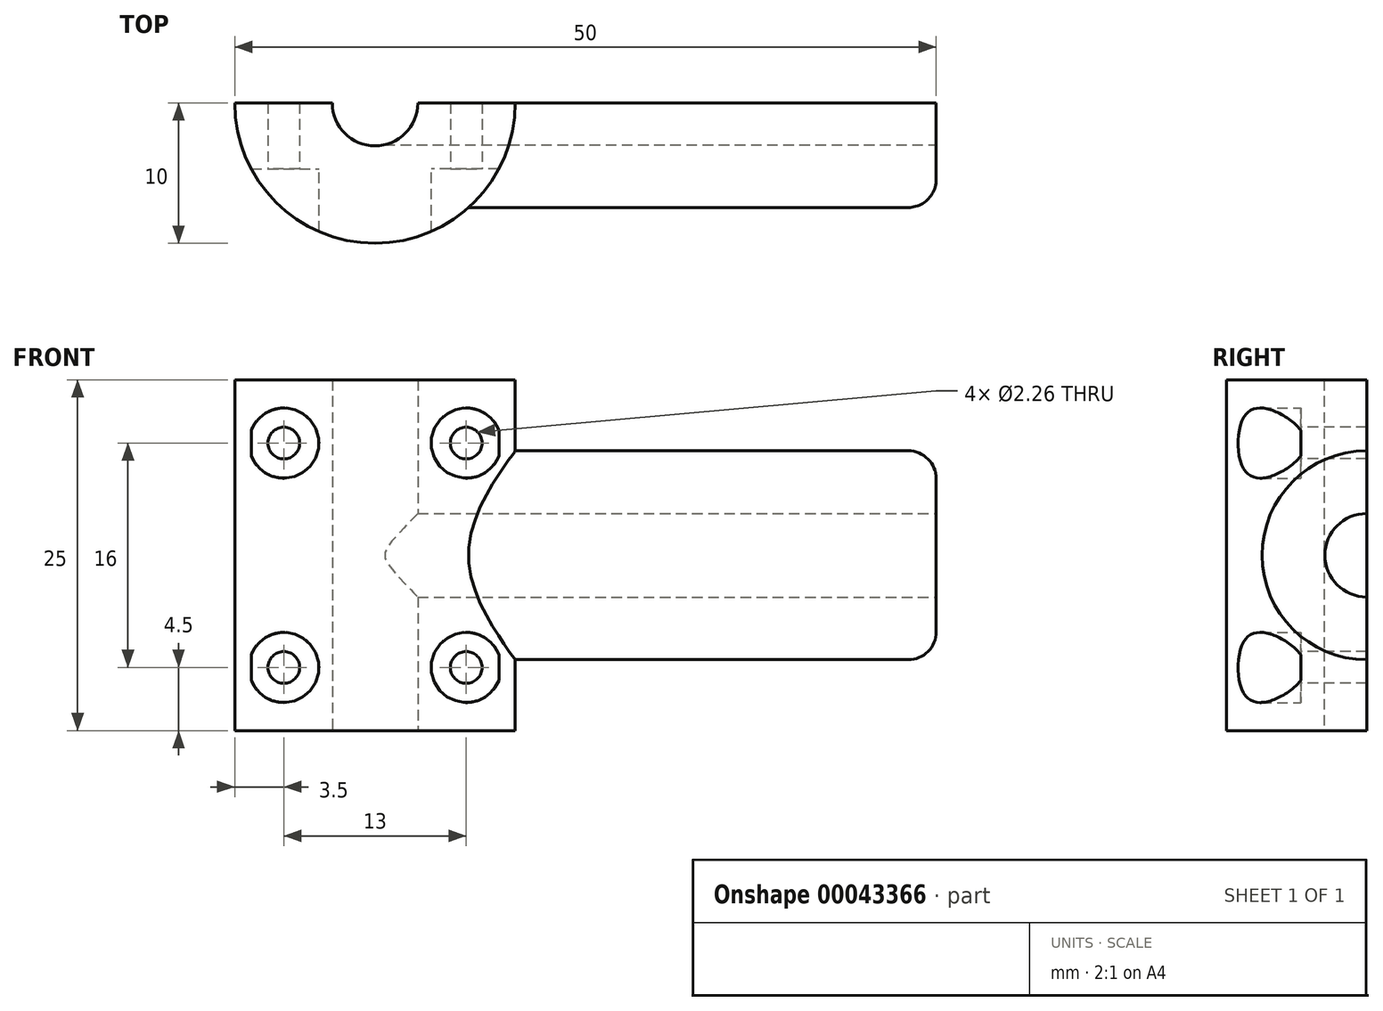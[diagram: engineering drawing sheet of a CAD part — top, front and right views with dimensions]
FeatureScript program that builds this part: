
annotation { "Feature Type Name" : "Feature", "Feature Type Description" : "" }
export const myFeature = defineFeature(function(context is Context, id is Id, definition is map)
    precondition{}
    {
        {
            var Q0;
            Q0=qCreatedBy(makeId("Top.planeOp"),FACE);
            var sketch = newSketch(context, id + "F0", { "sketchPlane" : qUnion([Q0])});
            skCircle(sketch, "E0", {"center": v(0, 0) * mm, "radius": 3.05 * mm});
            skCircle(sketch, "E1", {"center": v(0, 0) * mm, "radius": 10 * mm});
            skSolve(sketch);
        }
        {
            var Q0;
            Q0 = qSketchRegion(id + "F0", true);
            extrude(context, id + "F1", {"entities" : qUnion([Q0]), "depth" : 25 * mm, "symmetric" : true});
        }
        {
            var Q0;
            Q0=qCreatedBy(makeId("Right.planeOp"),FACE);
            cPlane(context, id + "F2", {"entities" : qUnion([Q0]), "cplaneType" : CPlaneType.OFFSET, "offset" : 40 * mm, "width" : 150 * mm, "height" : 150 * mm});
        }
        {
            var Q0;
            Q0=qCreatedBy(id+"F2.planeOp",FACE);
            var sketch = newSketch(context, id + "F3", { "sketchPlane" : qUnion([Q0])});
            skCircle(sketch, "E2", {"center": v(0, 0) * mm, "radius": 7.45 * mm});
            skSolve(sketch);
        }
        {
            var Q0;
            Q0 = qSketchRegion(id + "F3", true);
            extrude(context, id + "F4", {"entities" : qUnion([Q0]), "operationType" : NewBodyOperationType.ADD, "endBound" : BoundingType.UP_TO_NEXT, "oppositeDirection" : true, "depth" : 10.9 * mm});
        }
        {
            var Q0;
            Q0=makeQuery(id+"F4.opExtrude","CAP_FACE",FACE,{"disambiguationData":[OSD([sQuery(id+"F3.wireOp",EDGE,"E2")])],"isStart":true});
            var sketch = newSketch(context, id + "F5", { "sketchPlane" : qUnion([Q0])});
            skCircle(sketch, "E3", {"center": v(0, 0) * mm, "radius": 2.98 * mm});
            skSolve(sketch);
        }
        {
            var Q0;
            Q0 = qSketchRegion(id + "F5", true);
            extrude(context, id + "F6", {"entities" : qUnion([Q0]), "operationType" : NewBodyOperationType.REMOVE, "endBound" : BoundingType.UP_TO_NEXT, "oppositeDirection" : true, "depth" : 12.8 * mm});
        }
        {
            var Q0;
            Q0=makeQuery(id+"F4.opExtrude","CAP_EDGE",EDGE,{"disambiguationData":[OSD([sQuery(id+"F3.wireOp",EDGE,"E2")])],"isStart":true});
            fillet(context, id + "F7", {"entities" : qUnion([Q0]), "radius" : 2 * mm, "tangentPropagation" : true, "allowEdgeOverflow" : false});
        }
        {
            var Q0;
            Q0=qCreatedBy(makeId("Front.planeOp"),FACE);
            var sketch = newSketch(context, id + "F8", { "sketchPlane" : qUnion([Q0])});
            skCircle(sketch, "E4", {"center": v(-6.5, -8) * mm, "radius": 1.13 * mm});
            skLineSegment(sketch, "E5", {"start": v(0, 0) * mm, "end": v(0, -14.32) * mm, "construction": true});
            skCircle(sketch, "E6.MirrorC", {"center": v(6.5, -8) * mm, "radius": 1.13 * mm});
            skLineSegment(sketch, "E7", {"start": v(0, 0) * mm, "end": v(-19.65, 0) * mm, "construction": true});
            skCircle(sketch, "E8.MirrorC", {"center": v(-6.5, 8) * mm, "radius": 1.13 * mm});
            skCircle(sketch, "E9.MirrorC", {"center": v(6.5, 8) * mm, "radius": 1.13 * mm});
            skSolve(sketch);
        }
        {
            var Q0;
            Q0 = qSketchRegion(id + "F8", true);
            extrude(context, id + "F9", {"entities" : qUnion([Q0]), "operationType" : NewBodyOperationType.REMOVE, "oppositeDirection" : true, "depth" : 25 * mm, "symmetric" : true});
        }
        {
            var Q0;
            Q0=qCreatedBy(makeId("Front.planeOp"),FACE);
            cPlane(context, id + "F10", {"entities" : qUnion([Q0]), "cplaneType" : CPlaneType.OFFSET, "offset" : 4.7 * mm, "width" : 150 * mm, "height" : 150 * mm});
        }
        {
            var Q0;
            Q0=qCreatedBy(id+"F10.planeOp",FACE);
            var sketch = newSketch(context, id + "F11", { "sketchPlane" : qUnion([Q0])});
            skCircle(sketch, "E10", {"center": v(-6.5, 8) * mm, "radius": 2.5 * mm});
            skCircle(sketch, "E11", {"center": v(6.5, 8) * mm, "radius": 2.5 * mm});
            skCircle(sketch, "E12", {"center": v(-6.5, -8) * mm, "radius": 2.5 * mm});
            skCircle(sketch, "E13", {"center": v(6.5, -8) * mm, "radius": 2.5 * mm});
            skSolve(sketch);
        }
        {
            var Q0;
            Q0 = qSketchRegion(id + "F11", true);
            extrude(context, id + "F12", {"entities" : qUnion([Q0]), "operationType" : NewBodyOperationType.REMOVE, "depth" : 25 * mm});
        }
        {
            var Q0;
            Q0=qCreatedBy(makeId("Top.planeOp"),FACE);
            var sketch = newSketch(context, id + "F13", { "sketchPlane" : qUnion([Q0])});
            skLineSegment(sketch, "E14.bottom", {"start": v(-18.94, 0) * mm, "end": v(48.12, 0) * mm});
            skLineSegment(sketch, "E14.top", {"start": v(-18.94, 16.5) * mm, "end": v(48.12, 16.5) * mm});
            skLineSegment(sketch, "E14.left", {"start": v(-18.94, 0) * mm, "end": v(-18.94, 16.5) * mm});
            skLineSegment(sketch, "E14.right", {"start": v(48.12, 0) * mm, "end": v(48.12, 16.5) * mm});
            skSolve(sketch);
        }
        {
            var Q0;
            Q0 = qSketchRegion(id + "F13", true);
            extrude(context, id + "F14", {"entities" : qUnion([Q0]), "operationType" : NewBodyOperationType.REMOVE, "oppositeDirection" : true, "depth" : 25 * mm, "symmetric" : true});
        }
    });
